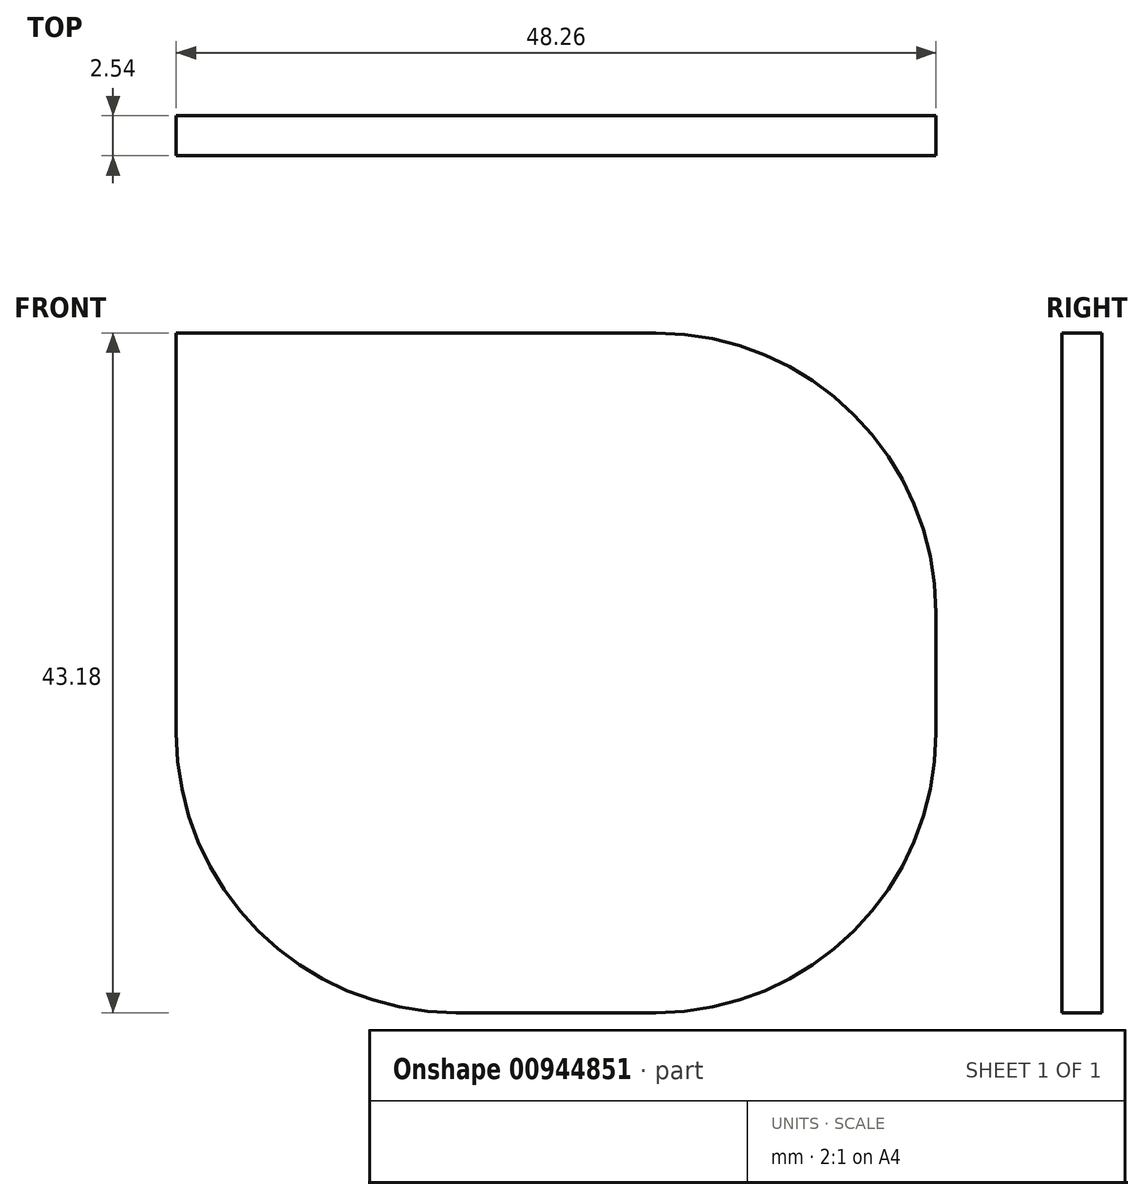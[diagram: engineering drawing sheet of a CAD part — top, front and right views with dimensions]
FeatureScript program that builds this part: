
annotation { "Feature Type Name" : "Feature", "Feature Type Description" : "" }
export const myFeature = defineFeature(function(context is Context, id is Id, definition is map)
    precondition{}
    {
        {
            var Q0;
            Q0=qCreatedBy(makeId("Front.planeOp"),FACE);
            var sketch = newSketch(context, id + "F0", { "sketchPlane" : qUnion([Q0])});
            skLineSegment(sketch, "E0.bottom", {"start": v(0, 0) * mm, "end": v(-48.26, 0) * mm});
            skLineSegment(sketch, "E0.top", {"start": v(0, 43.18) * mm, "end": v(-48.26, 43.18) * mm});
            skLineSegment(sketch, "E0.left", {"start": v(0, 0) * mm, "end": v(0, 43.18) * mm});
            skLineSegment(sketch, "E0.right", {"start": v(-48.26, 0) * mm, "end": v(-48.26, 43.18) * mm});
            skSolve(sketch);
        }
        {
            var Q0;
            Q0=makeQuery(id+"F0.imprint","IMPRINT",FACE,{"disambiguationData":[TD([[makeQuery(id+"F0.imprint","IMPRINT",EDGE,{"derivedFrom":sQuery(id+"F0.wireOp",EDGE,"E0.bottom")}),-1.0]])]});
            extrude(context, id + "F1", {"entities" : qUnion([Q0]), "depth" : 2.54 * mm, "offsetDistance" : 25.4 * mm});
        }
        {
            var Q0;
            Q0=makeQuery(id+"F1.opExtrude","SWEPT_EDGE",EDGE,{"disambiguationData":[OSD([sQuery(id+"F0.wireOp",EDGE,"E0.bottom"),sQuery(id+"F0.wireOp",EDGE,"E0.right")])]});
            var Q1;
            Q1=makeQuery(id+"F1.opExtrude","SWEPT_EDGE",EDGE,{"disambiguationData":[OSD([sQuery(id+"F0.wireOp",EDGE,"E0.bottom"),sQuery(id+"F0.wireOp",EDGE,"E0.left")])]});
            var Q2;
            Q2=makeQuery(id+"F1.opExtrude","SWEPT_EDGE",EDGE,{"disambiguationData":[OSD([sQuery(id+"F0.wireOp",EDGE,"E0.top"),sQuery(id+"F0.wireOp",EDGE,"E0.left")])]});
            fillet(context, id + "F2", {"entities" : qUnion([Q0, Q1, Q2]), "radius" : 17.78 * mm, "tangentPropagation" : true, "allowEdgeOverflow" : false});
        }
    });
